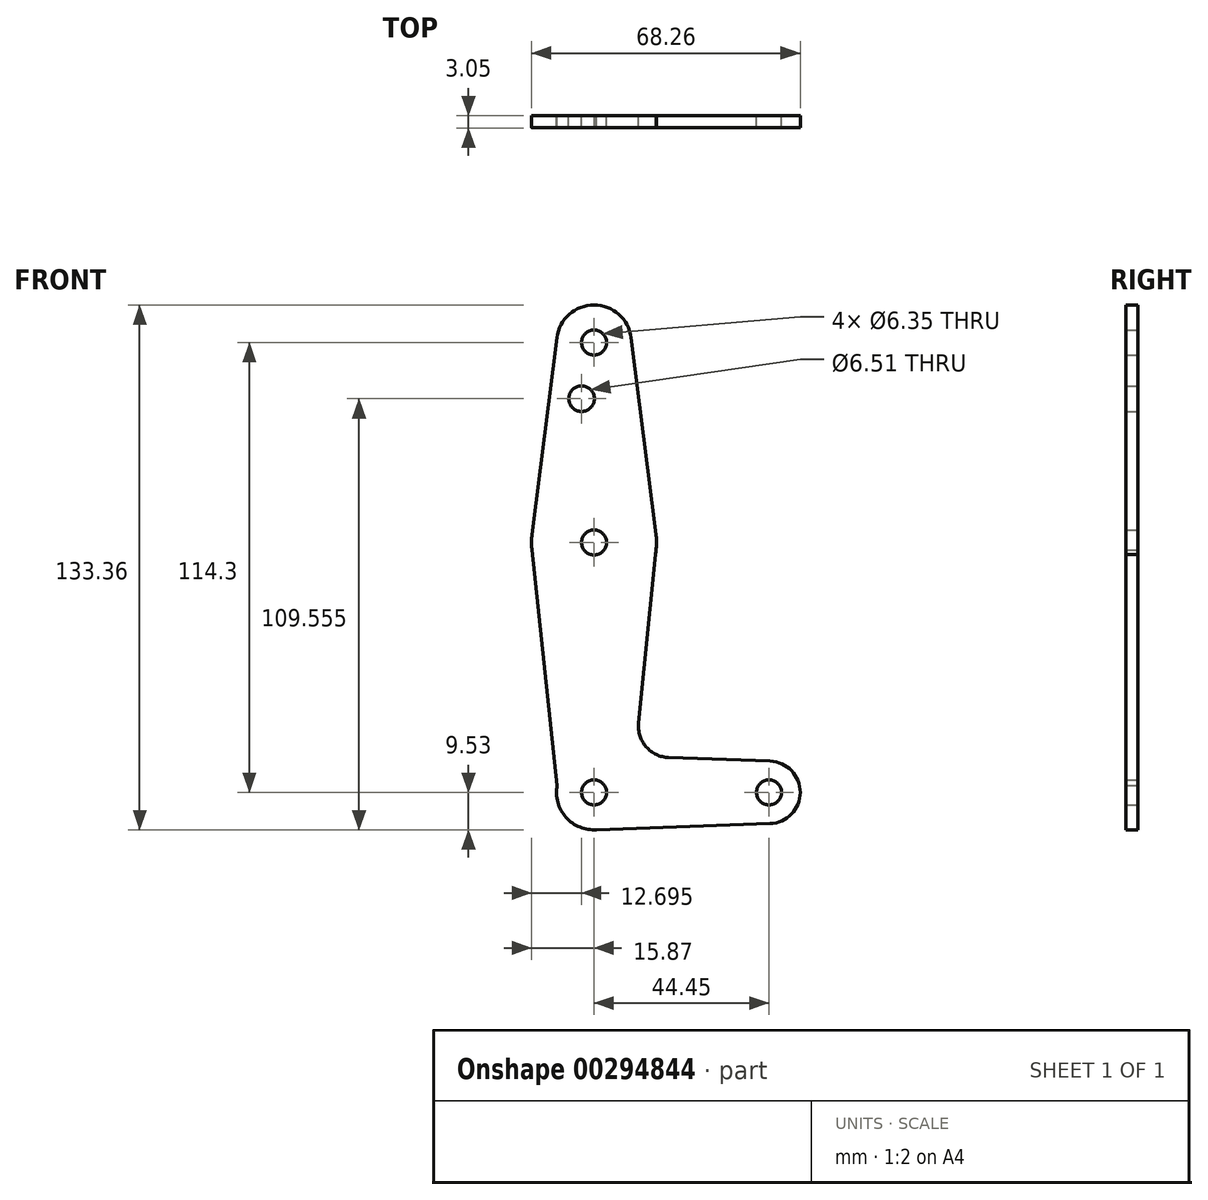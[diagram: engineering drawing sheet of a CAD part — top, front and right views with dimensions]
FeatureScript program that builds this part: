
annotation { "Feature Type Name" : "Feature", "Feature Type Description" : "" }
export const myFeature = defineFeature(function(context is Context, id is Id, definition is map)
    precondition{}
    {
        {
            var Q0;
            Q0=qCreatedBy(makeId("Front.planeOp"),FACE);
            var sketch = newSketch(context, id + "F0", { "sketchPlane" : qUnion([Q0])});
            skCircle(sketch, "E0", {"center": v(0, 0) * mm, "radius": 9.53 * mm});
            skCircle(sketch, "E1", {"center": v(44.45, 0) * mm, "radius": 7.94 * mm});
            skCircle(sketch, "E2", {"center": v(0, 63.5) * mm, "radius": 15.88 * mm});
            skCircle(sketch, "E3", {"center": v(0, 114.3) * mm, "radius": 9.53 * mm});
            skLineSegment(sketch, "E4", {"start": v(0, 114.3) * mm, "end": v(0, 0) * mm, "construction": true});
            skLineSegment(sketch, "E5", {"start": v(0, 0) * mm, "end": v(44.45, 0) * mm, "construction": true});
            skLineSegment(sketch, "E6", {"start": v(-9.45, 115.5) * mm, "end": v(-15.75, 65.48) * mm});
            skLineSegment(sketch, "E7", {"start": v(9.45, 115.5) * mm, "end": v(15.75, 65.48) * mm});
            skCircle(sketch, "E8", {"center": v(0, 114.3) * mm, "radius": 3.18 * mm});
            skCircle(sketch, "E9", {"center": v(-3.17, 100.03) * mm, "radius": 3.25 * mm});
            skCircle(sketch, "E10", {"center": v(0, 63.5) * mm, "radius": 3.18 * mm});
            skCircle(sketch, "E11", {"center": v(0, 0) * mm, "radius": 3.18 * mm});
            skCircle(sketch, "E12", {"center": v(44.45, 0) * mm, "radius": 3.18 * mm});
            skPoint(sketch, "E13.newPointA", {"position": v(9.57, 0) * mm});
            skLineSegment(sketch, "E14", {"start": v(15.57, 60.4) * mm, "end": v(11.32, 17.58) * mm});
            skLineSegment(sketch, "E15", {"start": v(18.95, 8.85) * mm, "end": v(44.73, 7.93) * mm});
            skLineSegment(sketch, "E16", {"start": v(0, -9.53) * mm, "end": v(44.73, -7.93) * mm});
            skArc(sketch, "E17.filletArc", {"start": v(11.32, 17.58) * mm, "mid": v(13.24, 11.56) * mm, "end": v(18.95, 8.85) * mm});
            skLineSegment(sketch, "E18", {"start": v(-15.75, 61.52) * mm, "end": v(-9.35, 1.8) * mm});
            skSolve(sketch);
        }
        {
            var Q0;
            Q0 = qSketchRegion(id + "F0", true);
            extrude(context, id + "F1", {"entities" : qUnion([Q0]), "depth" : 3.05 * mm});
        }
    });
